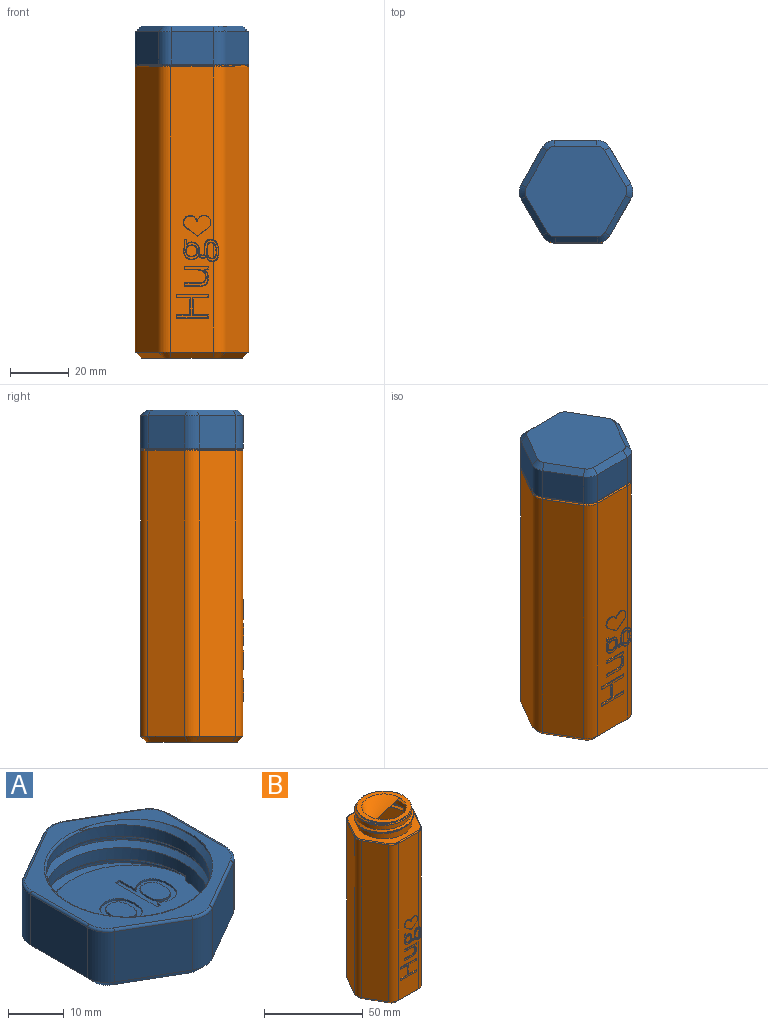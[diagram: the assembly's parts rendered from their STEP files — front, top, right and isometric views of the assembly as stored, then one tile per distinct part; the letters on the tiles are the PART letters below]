
ASSEMBLY  parts=2 mates=1
PART A: 133 faces, bbox 36.2x40.1x15.2 mm
  f0: plane 30.62x29.75mm, normal (0,0,1), area 522.3mm2, adj f1,f12,f13,f46,f47,f55,f56,f57
  f1: cylinder r=14.6mm len=29.2mm, axis (0,0,1), area 452.5mm2, adj f0,f10,f11,f12,f14,f45,f47
  f2: plane 12.5x11mm, normal (0.5,-0.87,0), area 158.8mm2, adj f15,f20,f25,f33
  f3: plane 14.43x11mm, normal (1,0,0), area 158.8mm2, adj f15,f16,f21,f36
  f4: plane 12.5x11mm, normal (0.5,0.87,0), area 158.8mm2, adj f16,f17,f24,f40
  f5: plane 12.5x11mm, normal (-0.5,0.87,0), area 158.8mm2, adj f17,f18,f28,f44
  f6: plane 14.43x11mm, normal (-1,0,0), area 158.8mm2, adj f18,f19,f32,f41
  f7: plane 12.5x11mm, normal (-0.5,-0.87,0), area 158.8mm2, adj f19,f20,f29,f37
  f8: plane 38.2x34.33mm, normal (0,0,1), area 275.1mm2, adj f10,f12,f13,f14,f21,f22,f23,f24
  f9: plane 34.87x31mm, normal (0,0,-1), area 829.3mm2, adj f33,f34,f35,f36,f37,f38,f39,f40
  f10: torus R=15mm, axis (0,0,1), area 32.4mm2, adj f1,f8,f12,f14
  f11: plane 0.91x0.9mm, normal (0,1,0), area 0.4mm2, adj f1,f45,f46,f47
  f12: bspline ~36.03x31.2mm, area 267.9mm2, adj f0,f1,f8,f10,f13
  f13: cylinder r=15.6mm len=31.2mm, axis (0,0,-1), area 97.9mm2, adj f0,f8,f12,f14,f46
  f14: bspline ~36.03x31.2mm, area 250.2mm2, adj f1,f8,f10,f13,f45,f46
  f15: cylinder r=5mm len=11mm, axis (0,0,-1), area 57.6mm2, adj f2,f3,f23,f34
  f16: cylinder r=5mm len=11mm, axis (0,0,-1), area 57.6mm2, adj f3,f4,f22,f38
  f17: cylinder r=5mm len=11mm, axis (0,0,-1), area 57.6mm2, adj f4,f5,f26,f42
  f18: cylinder r=5mm len=11mm, axis (0,0,-1), area 57.6mm2, adj f5,f6,f30,f43
  f19: cylinder r=5mm len=11mm, axis (0,0,-1), area 57.6mm2, adj f6,f7,f31,f39
  f20: cylinder r=5mm len=11mm, axis (0,0,-1), area 57.6mm2, adj f2,f7,f27,f35
  f21: cylinder r=0.5mm len=14.43mm, axis (0,-1,0), area 11.3mm2, adj f3,f8,f22,f23
  f22: torus R=4.5mm, axis (0,0,1), area 4mm2, adj f8,f16,f21,f24
  f23: torus R=4.5mm, axis (0,0,1), area 4mm2, adj f8,f15,f21,f25
  f24: cylinder r=0.5mm len=12.75mm, axis (0.87,-0.5,0), area 11.3mm2, adj f4,f8,f22,f26
  f25: cylinder r=0.5mm len=12.75mm, axis (-0.87,-0.5,0), area 11.3mm2, adj f2,f8,f23,f27
  f26: torus R=4.5mm, axis (0,0,1), area 4mm2, adj f8,f17,f24,f28
  f27: torus R=4.5mm, axis (0,0,1), area 4mm2, adj f8,f20,f25,f29
  f28: cylinder r=0.5mm len=12.75mm, axis (0.87,0.5,0), area 11.3mm2, adj f5,f8,f26,f30
  f29: cylinder r=0.5mm len=12.75mm, axis (-0.87,0.5,0), area 11.3mm2, adj f7,f8,f27,f31
  f30: torus R=4.5mm, axis (0,0,1), area 4mm2, adj f8,f18,f28,f32
  f31: torus R=4.5mm, axis (0,0,1), area 4mm2, adj f8,f19,f29,f32
  f32: cylinder r=0.5mm len=14.43mm, axis (0,1,0), area 11.3mm2, adj f6,f8,f30,f31
  f33: plane 13.5x8.95mm, normal (0.35,-0.61,-0.71), area 40.8mm2, adj f2,f9,f34,f35
  f34: cone r=3mm half-angle=45deg, axis (0,0,1), area 11.8mm2, adj f9,f15,f33,f36
  f35: cone r=3mm half-angle=45deg, axis (0,0,1), area 11.8mm2, adj f9,f20,f33,f37
  f36: plane 14.43x2mm, normal (0.71,0,-0.71), area 40.8mm2, adj f3,f9,f34,f38
  f37: plane 13.5x8.95mm, normal (-0.35,-0.61,-0.71), area 40.8mm2, adj f7,f9,f35,f39
  f38: cone r=3mm half-angle=45deg, axis (0,0,1), area 11.8mm2, adj f9,f16,f36,f40
  f39: cone r=3mm half-angle=45deg, axis (0,0,1), area 11.8mm2, adj f9,f19,f37,f41
  f40: plane 13.5x8.95mm, normal (0.35,0.61,-0.71), area 40.8mm2, adj f4,f9,f38,f42
  f41: plane 14.43x2mm, normal (-0.71,0,-0.71), area 40.8mm2, adj f6,f9,f39,f43
  f42: cone r=3mm half-angle=45deg, axis (0,0,1), area 11.8mm2, adj f9,f17,f40,f44
  f43: cone r=3mm half-angle=45deg, axis (0,0,1), area 11.8mm2, adj f9,f18,f41,f44
  f44: plane 13.5x8.95mm, normal (-0.35,0.61,-0.71), area 40.8mm2, adj f5,f9,f42,f43
  f45: bspline ~1.47x1.47mm, area 0.2mm2, adj f1,f11,f14,f46
  f46: cylinder r=0.1mm len=0.15mm, axis (0,0,-1), area 0mm2, adj f0,f11,f13,f14,f45,f47
  f47: cylinder r=0.1mm len=1mm, axis (-1,0,0), area 0.1mm2, adj f0,f1,f11,f46
  f48: extruded ~1.66x0.66mm, area 0.7mm2, adj f49,f70,f71,f130
  f49: extruded ~1.57x0.71mm, area 0.7mm2, adj f48,f50,f71,f130
  f50: extruded ~2.16x0.51mm, area 0.9mm2, adj f49,f51,f71,f130
  f51: extruded ~2.17x0.51mm, area 0.9mm2, adj f50,f52,f71,f130
  f52: extruded ~1.55x0.76mm, area 0.7mm2, adj f51,f53,f71,f130
  f53: extruded ~1.67x0.68mm, area 0.7mm2, adj f52,f54,f71,f130
  f54: extruded ~2.24x0.52mm, area 0.9mm2, adj f53,f70,f71,f130
  f55: extruded ~2.28x1mm, area 1mm2, adj f0,f56,f69,f71
  f56: extruded ~2.33x1.11mm, area 1.1mm2, adj f0,f55,f57,f71
  f57: plane 0.4x0.05mm, normal (0,-1,0), area 0mm2, adj f0,f56,f58,f71
  f58: extruded ~1.55x0.4mm, area 0.6mm2, adj f0,f57,f59,f71
  f59: plane 2.57x0.4mm, normal (-1,0,0), area 1mm2, adj f0,f58,f60,f71
  f60: plane 1.13x0.4mm, normal (0,-1,0), area 0.5mm2, adj f0,f59,f61,f71
  f61: plane 10.55x0.4mm, normal (1,0,0), area 4.2mm2, adj f0,f60,f62,f71
  f62: plane 0.81x0.4mm, normal (0,1,0), area 0.3mm2, adj f0,f61,f63,f71
  f63: plane 0.96x0.4mm, normal (-0.97,0.24,0), area 0.4mm2, adj f0,f62,f64,f71
  f64: plane 0.4x0.08mm, normal (0,1,0), area 0mm2, adj f0,f63,f65,f71
  f65: extruded ~1.01x0.83mm, area 0.5mm2, adj f0,f64,f66,f71
  f66: extruded ~1.33x0.4mm, area 0.5mm2, adj f0,f65,f67,f71
  f67: extruded ~2.27x1.01mm, area 1mm2, adj f0,f66,f68,f71
  f68: extruded ~2.85x0.82mm, area 1.2mm2, adj f0,f67,f69,f71
  f69: extruded ~2.83x0.81mm, area 1.2mm2, adj f0,f55,f68,f71
  f70: extruded ~2.23x0.51mm, area 0.9mm2, adj f48,f54,f71,f130
  f71: plane 10.69x6.55mm, normal (0,0,1), area 26.9mm2, adj f48,f49,f50,f51,f52,f53,f54,f55
  f72: extruded ~2.17x0.57mm, area 0.9mm2, adj f73,f88,f89,f131
  f73: extruded ~2.16x0.56mm, area 0.9mm2, adj f72,f74,f89,f131
  f74: extruded ~1.67x0.73mm, area 0.8mm2, adj f73,f75,f89,f131
  f75: extruded ~1.69x0.74mm, area 0.8mm2, adj f74,f76,f89,f131
  f76: extruded ~2.15x0.57mm, area 0.9mm2, adj f75,f77,f89,f131
  f77: extruded ~2.17x0.57mm, area 0.9mm2, adj f76,f78,f89,f131
  f78: extruded ~1.68x0.74mm, area 0.8mm2, adj f77,f88,f89,f131
  f79: extruded ~2.84x0.91mm, area 1.2mm2, adj f0,f80,f87,f89
  f80: extruded ~2.81x0.92mm, area 1.2mm2, adj f0,f79,f81,f89
  f81: extruded ~2.48x1.04mm, area 1.1mm2, adj f0,f80,f82,f89
  f82: extruded ~2.52x1.01mm, area 1.1mm2, adj f0,f81,f83,f89
  f83: extruded ~2.83x0.91mm, area 1.2mm2, adj f0,f82,f84,f89
  f84: extruded ~2.05x0.42mm, area 0.8mm2, adj f0,f83,f85,f89
  f85: extruded ~1.34x1.19mm, area 0.7mm2, adj f0,f84,f86,f89
  f86: extruded ~1.77x0.47mm, area 0.7mm2, adj f0,f85,f87,f89
  f87: extruded ~2.53x1.02mm, area 1.1mm2, adj f0,f79,f86,f89
  f88: extruded ~1.67x0.75mm, area 0.8mm2, adj f72,f78,f89,f131
  f89: plane 7.71x6.83mm, normal (0,0,1), area 21.2mm2, adj f72,f73,f74,f75,f76,f77,f78,f79
  f90: plane 1.58x0.4mm, normal (0,-1,0), area 0.6mm2, adj f91,f107,f108,f132
  f91: plane 3.79x0.4mm, normal (-1,0,0), area 1.5mm2, adj f90,f92,f108,f132
  f92: plane 1.5x0.4mm, normal (0,1,0), area 0.6mm2, adj f91,f93,f108,f132
  f93: extruded ~1.86x0.43mm, area 0.8mm2, adj f92,f94,f108,f132
  f94: extruded ~1.42x0.58mm, area 0.6mm2, adj f93,f95,f108,f132
  f95: extruded ~1.46x0.57mm, area 0.6mm2, adj f94,f107,f108,f132
  f96: plane 4.12x0.4mm, normal (-1,0,0), area 1.6mm2, adj f0,f97,f106,f108
  f97: plane 2.07x0.4mm, normal (0,1,0), area 0.8mm2, adj f0,f96,f98,f108
  f98: plane 4.12x2.4mm, normal (0.86,0.5,0), area 1.9mm2, adj f0,f97,f99,f108
  f99: plane 1.36x0.4mm, normal (0,1,0), area 0.5mm2, adj f0,f98,f100,f108
  f100: plane 4.46x2.69mm, normal (-0.86,-0.52,0), area 2.1mm2, adj f0,f99,f101,f108
  f101: extruded ~2.66x1.99mm, area 1.4mm2, adj f0,f100,f102,f108
  f102: extruded ~2.1x0.87mm, area 0.9mm2, adj f0,f101,f103,f108
  f103: extruded ~2.7x0.7mm, area 1.1mm2, adj f0,f102,f104,f108
  f104: plane 2.72x0.4mm, normal (0,-1,0), area 1.1mm2, adj f0,f103,f105,f108
  f105: plane 9.92x0.4mm, normal (1,0,0), area 4mm2, adj f0,f104,f106,f108
  f106: plane 1.15x0.4mm, normal (0,1,0), area 0.5mm2, adj f0,f96,f105,f108
  f107: extruded ~1.79x0.49mm, area 0.8mm2, adj f90,f95,f108,f132
  f108: plane 9.92x6.99mm, normal (0,0,1), area 29.5mm2, adj f90,f91,f92,f93,f94,f95,f96,f97
  f109: plane 3.37x0.4mm, normal (0,-1,0), area 1.3mm2, adj f0,f110,f128,f129
  f110: plane 1.03x0.4mm, normal (1,0,0), area 0.4mm2, adj f0,f109,f111,f129
  f111: plane 2.22x0.4mm, normal (0,1,0), area 0.9mm2, adj f0,f110,f112,f129
  f112: plane 3.05x0.4mm, normal (1,0,0), area 1.2mm2, adj f0,f111,f113,f129
  f113: extruded ~2.01x0.4mm, area 0.8mm2, adj f0,f112,f114,f129
  f114: extruded ~2.88x1.04mm, area 1.3mm2, adj f0,f113,f115,f129
  f115: extruded ~3.04x0.98mm, area 1.3mm2, adj f0,f114,f116,f129
  f116: extruded ~2.99x1.02mm, area 1.3mm2, adj f0,f115,f117,f129
  f117: extruded ~2.83x1.08mm, area 1.2mm2, adj f0,f116,f118,f129
  f118: extruded ~2.58x0.57mm, area 1.1mm2, adj f0,f117,f119,f129
  f119: plane 1.02x0.45mm, normal (-0.92,0.4,0), area 0.4mm2, adj f0,f118,f120,f129
  f120: extruded ~2.96x0.58mm, area 1.2mm2, adj f0,f119,f121,f129
  f121: extruded ~2.73x0.61mm, area 1.1mm2, adj f0,f120,f122,f129
  f122: extruded ~1.79x1.78mm, area 1mm2, adj f0,f121,f123,f129
  f123: extruded ~2.71x0.62mm, area 1.1mm2, adj f0,f122,f124,f129
  f124: extruded ~3.75x1.25mm, area 1.6mm2, adj f0,f123,f125,f129
  f125: extruded ~3.5x1.34mm, area 1.5mm2, adj f0,f124,f126,f129
  f126: extruded ~1.89x0.4mm, area 0.8mm2, adj f0,f125,f127,f129
  f127: extruded ~1.6x0.4mm, area 0.7mm2, adj f0,f126,f128,f129
  f128: plane 4.82x0.4mm, normal (-1,0,0), area 1.9mm2, adj f0,f109,f127,f129
  f129: plane 10.19x8.25mm, normal (0,0,1), area 29.8mm2, adj f109,f110,f111,f112,f113,f114,f115,f116
  f130: plane 5.81x4.25mm, normal (0,0,1), area 20.8mm2, adj f48,f49,f50,f51,f52,f53,f54,f70
  f131: plane 5.81x4.5mm, normal (0,0,1), area 21.7mm2, adj f72,f73,f74,f75,f76,f77,f78,f88
  f132: plane 3.94x3.79mm, normal (0,0,1), area 13.5mm2, adj f90,f91,f92,f93,f94,f95,f107
PART B: 144 faces, bbox 40x36.1x111.1 mm
  f0: plane 97.75x14.69mm, normal (0,-1,0), area 1253.1mm2, adj f20,f21,f39,f54,f64,f65,f67,f68
  f1: plane 5.49x2.17mm, normal (0,-1,0), area 9.1mm2, adj f21,f76,f77,f78,f80,f82,f83,f84
  f2: bspline ~34.64x30mm, area 206.1mm2, adj f12,f15,f19,f32
  f3: cylinder r=15mm len=30mm, axis (0,0,-1), area 44.4mm2, adj f15,f18,f29,f32,f33
  f4: bspline ~34.64x30mm, area 182.1mm2, adj f12,f15,f17,f29,f30
  f5: plane 97.5x12.5mm, normal (-0.87,-0.5,0), area 1407.3mm2, adj f20,f25,f43,f50
  f6: plane 97.5x12.5mm, normal (0.87,-0.5,0), area 1407.3mm2, adj f21,f22,f35,f58
  f7: plane 97.5x12.5mm, normal (0.87,0.5,0), area 1407.3mm2, adj f22,f23,f38,f55
  f8: plane 97.5x14.43mm, normal (0,1,0), area 1407.3mm2, adj f23,f24,f42,f51
  f9: plane 97.5x12.5mm, normal (-0.87,0.5,0), area 1407.3mm2, adj f24,f25,f46,f47
  f10: plane 37.87x34mm, normal (0,0,1), area 378.8mm2, adj f12,f35,f36,f37,f38,f39,f40,f41
  f11: plane 34.87x31mm, normal (0,0,-1), area 829.3mm2, adj f47,f48,f49,f50,f51,f52,f53,f54
  f12: cylinder r=14mm len=28mm, axis (0,0,-1), area 489.8mm2, adj f2,f4,f10,f14,f15,f17,f19
  f13: plane 27.6x27.6mm, normal (0,0,1), area 200mm2, adj f14,f28
  f14: torus R=13.8mm, axis (0,0,1), area 27.5mm2, adj f12,f13,f16
  f15: plane 2.5x1mm, normal (0,-1,0), area 1.5mm2, adj f2,f3,f4,f12,f29,f32
  f16: plane 15.47x14.77mm, normal (0,0,1), area 8.2mm2, adj f14,f17,f18,f19
  f17: bspline ~17.22x4.15mm, area 4.2mm2, adj f4,f12,f16,f31
  f18: torus R=14.6mm, axis (0,0,1), area 2.1mm2, adj f3,f16,f30,f31,f34
  f19: bspline ~19.85x4.5mm, area 15.5mm2, adj f2,f12,f16,f33,f34
  f20: cylinder r=5mm len=97.5mm, axis (0,0,-1), area 510.5mm2, adj f0,f5,f41,f52
  f21: cylinder r=5mm len=97.5mm, axis (0,0,-1), area 510.5mm2, adj f0,f1,f6,f37,f56,f61
  f22: cylinder r=5mm len=97.5mm, axis (0,0,-1), area 510.5mm2, adj f6,f7,f36,f57
  f23: cylinder r=5mm len=97.5mm, axis (0,0,-1), area 510.5mm2, adj f7,f8,f40,f53
  f24: cylinder r=5mm len=97.5mm, axis (0,0,-1), area 510.5mm2, adj f8,f9,f44,f49
  f25: cylinder r=5mm len=97.5mm, axis (0,0,-1), area 510.5mm2, adj f5,f9,f45,f48
  f26: plane 25.87x25.87mm, normal (0,0,1), area 525.5mm2, adj f143
  f27: cylinder r=14.93mm len=63mm, axis (0,0,-1), area 5911.4mm2, adj f28,f143
  f28: cone r=14.93mm half-angle=5deg, axis (0,0,-1), area 3469.3mm2, adj f13,f27
  f29: bspline ~30.01x30.01mm, area 29.6mm2, adj f3,f4,f15,f30
  f30: bspline ~1.03x0.92mm, area 0.1mm2, adj f4,f18,f29,f31
  f31: bspline ~0.22x0.18mm, area 0mm2, adj f17,f18,f30
  f32: bspline ~30.01x30.01mm, area 30.3mm2, adj f2,f3,f15,f33
  f33: bspline ~0.82x0.74mm, area 0.1mm2, adj f3,f19,f32,f34
  f34: bspline ~0.49x0.33mm, area 0mm2, adj f18,f19,f33
  f35: cylinder r=0.5mm len=12.75mm, axis (-0.5,-0.87,0), area 11.3mm2, adj f6,f10,f36,f37
  f36: torus R=4.5mm, axis (0,0,1), area 4mm2, adj f10,f22,f35,f38
  f37: torus R=4.5mm, axis (0,0,1), area 4mm2, adj f10,f21,f35,f39
  f38: cylinder r=0.5mm len=12.75mm, axis (0.5,-0.87,0), area 11.3mm2, adj f7,f10,f36,f40
  f39: cylinder r=0.5mm len=14.43mm, axis (-1,0,0), area 11.3mm2, adj f0,f10,f37,f41
  f40: torus R=4.5mm, axis (0,0,1), area 4mm2, adj f10,f23,f38,f42
  f41: torus R=4.5mm, axis (0,0,1), area 4mm2, adj f10,f20,f39,f43
  f42: cylinder r=0.5mm len=14.43mm, axis (1,0,0), area 11.3mm2, adj f8,f10,f40,f44
  f43: cylinder r=0.5mm len=12.75mm, axis (-0.5,0.87,0), area 11.3mm2, adj f5,f10,f41,f45
  f44: torus R=4.5mm, axis (0,0,1), area 4mm2, adj f10,f24,f42,f46
  f45: torus R=4.5mm, axis (0,0,1), area 4mm2, adj f10,f25,f43,f46
  f46: cylinder r=0.5mm len=12.75mm, axis (0.5,0.87,0), area 11.3mm2, adj f9,f10,f44,f45
  f47: plane 13.5x8.95mm, normal (-0.61,0.35,-0.71), area 40.8mm2, adj f9,f11,f48,f49
  f48: cone r=3mm half-angle=45deg, axis (0,0,1), area 11.8mm2, adj f11,f25,f47,f50
  f49: cone r=3mm half-angle=45deg, axis (0,0,1), area 11.8mm2, adj f11,f24,f47,f51
  f50: plane 13.5x8.95mm, normal (-0.61,-0.35,-0.71), area 40.8mm2, adj f5,f11,f48,f52
  f51: plane 14.43x2mm, normal (0,0.71,-0.71), area 40.8mm2, adj f8,f11,f49,f53
  f52: cone r=3mm half-angle=45deg, axis (0,0,1), area 11.8mm2, adj f11,f20,f50,f54
  f53: cone r=3mm half-angle=45deg, axis (0,0,1), area 11.8mm2, adj f11,f23,f51,f55
  f54: plane 14.43x2mm, normal (0,-0.71,-0.71), area 40.8mm2, adj f0,f11,f52,f56
  f55: plane 13.5x8.95mm, normal (0.61,0.35,-0.71), area 40.8mm2, adj f7,f11,f53,f57
  f56: cone r=3mm half-angle=45deg, axis (0,0,1), area 11.8mm2, adj f11,f21,f54,f58
  f57: cone r=3mm half-angle=45deg, axis (0,0,1), area 11.8mm2, adj f11,f22,f55,f58
  f58: plane 13.5x8.95mm, normal (0.61,-0.35,-0.71), area 40.8mm2, adj f6,f11,f56,f57
  f59: plane 10.51x7.88mm, normal (0,-1,0), area 22.7mm2, adj f131,f132,f133,f134,f135,f136,f137,f138
  f60: plane 8.09x6.61mm, normal (0,-1,0), area 15.8mm2, adj f114,f115,f116,f117,f118,f119,f120,f121
  f61: plane 7.63x2.11mm, normal (0,1,0), area 7.6mm2, adj f21,f77,f79,f81,f83,f85,f86,f87
  f62: plane 11.81x7.54mm, normal (0,-1,0), area 23.8mm2, adj f70,f71,f72,f73,f74,f75,f76,f77
  f63: plane 3.76x3.72mm, normal (0,-1,0), area 10.9mm2, adj f70,f71,f72,f73,f74,f75
  f64: plane 3.78x2.83mm, normal (0.6,0,-0.8), area 0.9mm2, adj f0,f65,f66,f67
  f65: cylinder r=2.36mm len=4.68mm, axis (0,1,0), area 1.8mm2, adj f0,f64,f66,f69
  f66: plane 9.24x6.96mm, normal (0,-1,0), area 42.3mm2, adj f64,f65,f67,f68,f69
  f67: plane 3.94x2.99mm, normal (-0.42,-0.71,-0.57), area 1.3mm2, adj f0,f64,f66,f68
  f68: cone r=2.16mm half-angle=45deg, axis (0,1,0), area 2.4mm2, adj f0,f66,f67,f69
  f69: cone r=0.12mm half-angle=45deg, axis (0,-1,0), area 0.1mm2, adj f0,f65,f66,f68
  f70: bspline ~2.02x1.96mm, area 0.9mm2, adj f62,f63,f71,f72
  f71: bspline ~2.04x2.04mm, area 0.9mm2, adj f62,f63,f70,f73
  f72: bspline ~1.49x0.64mm, area 0.4mm2, adj f62,f63,f70,f74
  f73: bspline ~1.49x0.67mm, area 0.4mm2, adj f62,f63,f71,f75
  f74: bspline ~1.45x0.69mm, area 0.4mm2, adj f62,f63,f72,f75
  f75: bspline ~1.54x0.67mm, area 0.4mm2, adj f62,f63,f73,f74
  f76: bspline ~1.09x0.62mm, area 0.3mm2, adj f1,f62,f77,f78
  f77: bspline ~1.43x0.97mm, area 0.5mm2, adj f1,f61,f62,f76,f79
  f78: bspline ~1.65x0.46mm, area 0.5mm2, adj f1,f62,f76,f80
  f79: bspline ~2.41x0.67mm, area 0.7mm2, adj f61,f62,f77,f81
  f80: plane 1.49x0.2mm, normal (0.71,-0.71,0), area 0.4mm2, adj f1,f62,f78,f82
  f81: bspline ~1.71x0.54mm, area 0.5mm2, adj f61,f62,f79,f83
  f82: bspline ~1.44x0.6mm, area 0.4mm2, adj f1,f62,f80,f84
  f83: bspline ~1.18x0.76mm, area 0.4mm2, adj f1,f61,f62,f81,f84
  f84: bspline ~1.31x0.68mm, area 0.4mm2, adj f1,f62,f82,f83
  f85: bspline ~3.18x0.88mm, area 0.9mm2, adj f61,f62,f86,f87
  f86: bspline ~2.07x1.2mm, area 0.7mm2, adj f0,f61,f62,f85,f88
  f87: bspline ~2.47x0.76mm, area 0.7mm2, adj f61,f62,f85,f89
  f88: bspline ~1.63x0.85mm, area 0.5mm2, adj f0,f62,f86,f90
  f89: bspline ~1.69x1.01mm, area 0.5mm2, adj f0,f61,f62,f87,f91
  f90: bspline ~2.04x0.72mm, area 0.6mm2, adj f0,f62,f88,f92
  f91: bspline ~1.29x0.64mm, area 0.4mm2, adj f0,f62,f89,f93
  f92: plane 1.45x0.2mm, normal (-0.71,-0.71,0), area 0.4mm2, adj f0,f62,f90,f94
  f93: bspline ~1.97x1mm, area 0.5mm2, adj f0,f62,f91,f95
  f94: bspline ~1.05x0.36mm, area 0.3mm2, adj f0,f62,f92,f96
  f95: bspline ~1.21x0.83mm, area 0.3mm2, adj f0,f62,f93,f97
  f96: bspline ~0.67x0.48mm, area 0.2mm2, adj f0,f62,f94,f98
  f97: bspline ~0.69x0.38mm, area 0.2mm2, adj f0,f62,f95,f99
  f98: bspline ~1.26x1.05mm, area 0.4mm2, adj f0,f62,f96,f100
  f99: bspline ~0.78x0.41mm, area 0.2mm2, adj f0,f62,f97,f101
  f100: bspline ~0.79x0.28mm, area 0.2mm2, adj f0,f62,f98,f102
  f101: bspline ~1.25x1.01mm, area 0.3mm2, adj f0,f62,f99,f103
  f102: bspline ~2.25x0.87mm, area 0.7mm2, adj f0,f62,f100,f104
  f103: bspline ~1.48x1.14mm, area 0.4mm2, adj f0,f62,f101,f105
  f104: bspline ~1.92x0.97mm, area 0.6mm2, adj f0,f62,f102,f106
  f105: bspline ~1.43x0.57mm, area 0.4mm2, adj f0,f62,f103,f107
  f106: bspline ~0.95x0.35mm, area 0.3mm2, adj f0,f62,f104,f108
  f107: bspline ~2.07x0.95mm, area 0.6mm2, adj f0,f62,f105,f109
  f108: bspline ~1.08x0.79mm, area 0.3mm2, adj f0,f62,f106,f110
  f109: bspline ~2.28x0.88mm, area 0.7mm2, adj f0,f62,f107,f111
  f110: plane 1.9x0.36mm, normal (0.7,-0.71,0.08), area 0.5mm2, adj f0,f62,f108,f112
  f111: bspline ~1.24x0.37mm, area 0.3mm2, adj f0,f62,f109,f113
  f112: plane 0.78x0.2mm, normal (0,-0.71,0.71), area 0.2mm2, adj f0,f62,f110,f113
  f113: plane 2.85x0.2mm, normal (-0.71,-0.71,0), area 0.8mm2, adj f0,f62,f111,f112
  f114: plane 1.02x0.2mm, normal (0.71,-0.71,0), area 0.2mm2, adj f0,f60,f115,f116
  f115: plane 8.18x0.2mm, normal (0,-0.71,0.71), area 2.3mm2, adj f0,f60,f114,f117
  f116: plane 1.3x0.35mm, normal (0.11,-0.71,-0.7), area 0.3mm2, adj f0,f60,f114,f118
  f117: plane 1.24x0.2mm, normal (-0.71,-0.71,0), area 0.3mm2, adj f0,f60,f115,f119
  f118: plane 0.35x0.2mm, normal (0.71,-0.71,0), area 0.1mm2, adj f0,f60,f116,f120
  f119: plane 4.3x0.2mm, normal (0,-0.71,-0.71), area 1.2mm2, adj f0,f60,f117,f121
  f120: bspline ~1.24x1.19mm, area 0.4mm2, adj f0,f60,f118,f122
  f121: bspline ~2.42x0.79mm, area 0.7mm2, adj f0,f60,f119,f123
  f122: bspline ~1.54x0.5mm, area 0.4mm2, adj f0,f60,f120,f124
  f123: bspline ~2.03x0.91mm, area 0.6mm2, adj f0,f60,f121,f125
  f124: bspline ~2.23x0.85mm, area 0.7mm2, adj f0,f60,f122,f126
  f125: bspline ~1.57x0.69mm, area 0.5mm2, adj f0,f60,f123,f127
  f126: bspline ~2.27x0.88mm, area 0.7mm2, adj f0,f60,f124,f128
  f127: bspline ~1.63x0.65mm, area 0.5mm2, adj f0,f60,f125,f129
  f128: plane 5.35x0.2mm, normal (0,-0.71,-0.71), area 1.5mm2, adj f0,f60,f126,f130
  f129: plane 5.3x0.2mm, normal (0,-0.71,0.71), area 1.5mm2, adj f0,f60,f127,f130
  f130: plane 1.25x0.2mm, normal (-0.71,-0.71,0), area 0.3mm2, adj f0,f60,f128,f129
  f131: plane 10.91x0.2mm, normal (0,-0.71,-0.71), area 3mm2, adj f0,f59,f132,f133
  f132: plane 1.27x0.2mm, normal (-0.71,-0.71,0), area 0.3mm2, adj f0,f59,f131,f134
  f133: plane 1.27x0.2mm, normal (0.71,-0.71,0), area 0.3mm2, adj f0,f59,f131,f135
  f134: plane 4.84x0.2mm, normal (0,-0.71,0.71), area 1.3mm2, adj f0,f59,f132,f136
  f135: plane 5.33x0.2mm, normal (0,-0.71,0.71), area 1.5mm2, adj f0,f59,f133,f137
  f136: plane 6.15x0.2mm, normal (-0.71,-0.71,0), area 1.7mm2, adj f0,f59,f134,f138
  f137: plane 6.15x0.2mm, normal (0.71,-0.71,0), area 1.7mm2, adj f0,f59,f135,f139
  f138: plane 4.84x0.2mm, normal (0,-0.71,-0.71), area 1.3mm2, adj f0,f59,f136,f140
  f139: plane 5.33x0.2mm, normal (0,-0.71,-0.71), area 1.5mm2, adj f0,f59,f137,f141
  f140: plane 1.27x0.2mm, normal (-0.71,-0.71,0), area 0.3mm2, adj f0,f59,f138,f142
  f141: plane 1.27x0.2mm, normal (0.71,-0.71,0), area 0.3mm2, adj f0,f59,f139,f142
  f142: plane 10.91x0.2mm, normal (0,-0.71,0.71), area 3mm2, adj f0,f59,f140,f141
  f143: cone r=14.93mm half-angle=45deg, axis (0,0,1), area 247.6mm2, adj f26,f27
PLACE A rot(axis=(0.71,-0.71,0),180deg) t=(-91.85,-93.61,98.79)mm
PLACE B t=(-91.85,-93.61,-14.71)mm fixed
MATE revolute B.f3 <-> A.f1  axis (0,0,1) through (-91.85,-93.61,95.29)mm
